# Revit family: NBS_wediSystemsUKLtd_Stng_SanoasaComoda_BenchElement
name_source: partatom
category: Furniture
revit_build: Autodesk Revit 2018 (Build: 20190510_1515(x64)
units: mm (PartAtom-declared; Revit-internal decimal feet)

## family parameters
Always vertical = Yes
Cut with Voids When Loaded = No
Room Calculation Point = No
Shared = No
Work Plane-Based = No

## types (2) — shared parameters
AssetType = Fixed
BenchMaterial = NBS_Concept
Category = Pr_40_20_06_83:Shower seats
Color = Grey
Description = wedi Sanoasa Comoda, bench element, slope to front
DurationUnit = year
ExpectedLife = 30
Features = Sanoasa Comoda benches are available in so many different designs, meaning that they can be built into almost any seating combination
Finish = resistant and glass fibre reinforced cement coating
Form = Practical wellness benches with modular construction
IfcExportAs = IfcFurnitureType
IfcExportType = SOFA
IsBuiltIn = Yes
MainColor = Grey
ManufacturerName = wedi Systems (UK) Ltd
ManufacturerURL = https://www.wedi.de
Material = A waterproof extruded polystyrene rigid foam core with a special, resistant and glass fibre reinforced cement coating
MaterialsFrame = A waterproof extruded polystyrene rigid foam core with a special, resistant and glass fibre reinforced cement coating
MaterialsSeat = A waterproof extruded polystyrene rigid foam core with a special, resistant and glass fibre reinforced cement coating
ModelReference = wedi Sanoasa Comoda
NBSCertification = www.nationalbimlibrary.com/cert/kb5dqbrx
NBSDescription = Seating
NBSReference = 45-35-72/352
Name = Seating_wediSanoasaComodaBenchElement_wediSystemsLtd
NominalDepth = 600 mm
NominalHeight = 620 mm  [stored 2.03412 ft]
ProductInformation = https://www.wedi.de
Status = UNSET
Style = Bench element
Uniclass2015Code = Pr_40_20_06_83
Uniclass2015Title = Shower seats
Uniclass2015Version = Products v1.14
Version = 2
WarrantyDescription = available on request
WarrantyDurationUnit = year

## per-type parameters (varying)
| type | BIMObjectName | ModelNumber | NominalLength | NominalWidth | Size |
| BenchElement_SlopeToFront_1000mm | NBS_wediSystemsUKLtd_Seating_SanoasaComoda_BenchElement_SlopeToFront_1000mm | 076447015 | 1000 mm  [stored 3.28084 ft] | 1000 mm  [stored 3.28084 ft] | 600 x 1000 x 620 mm |
| BenchElement_SlopeToFront_2000mm | NBS_wediSystemsUKLtd_Seating_SanoasaComoda_BenchElement_SlopeToFront_2000mm | 076438000 | 2000 mm  [stored 6.56168 ft] | 2000 mm  [stored 6.56168 ft] | 600 x 2000 x 620 mm |

note: [stored X ft] marks values corroborated as IEEE doubles in the binary element streams (Revit-internal decimal feet)

## geometry (parser evidence)
native form markers: Sweep x3
no freeform markers — native parametric forms only
